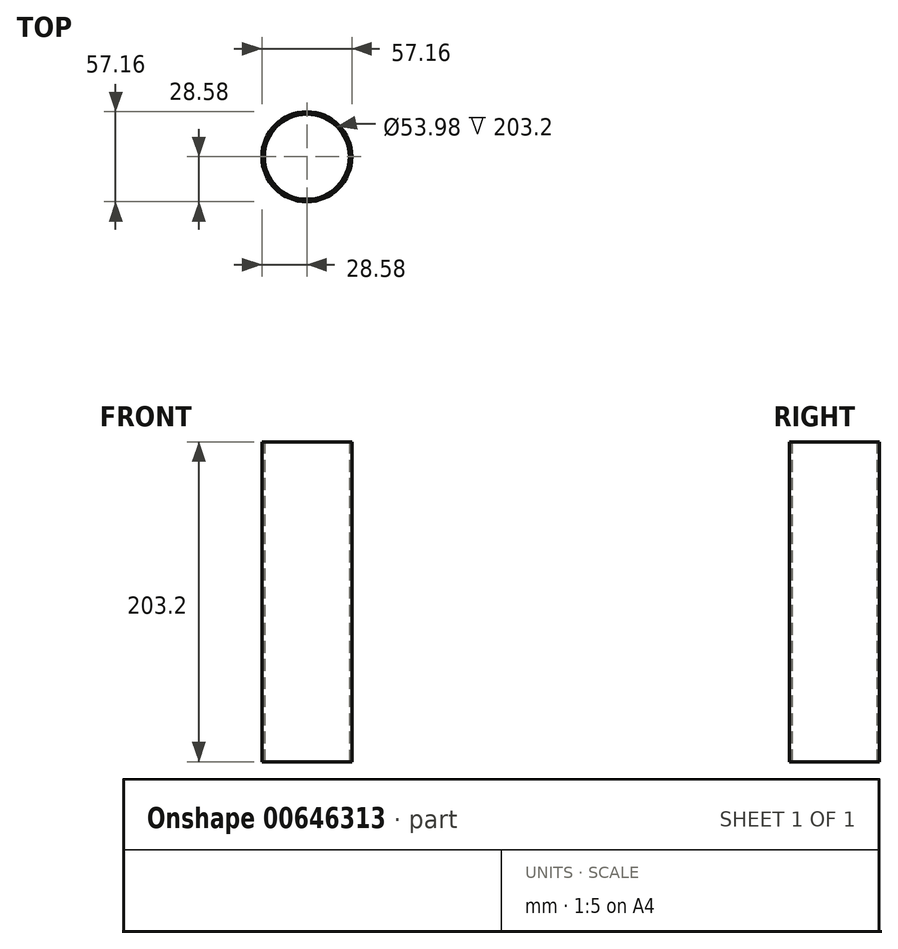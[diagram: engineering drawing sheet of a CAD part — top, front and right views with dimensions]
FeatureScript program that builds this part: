
annotation { "Feature Type Name" : "Feature", "Feature Type Description" : "" }
export const myFeature = defineFeature(function(context is Context, id is Id, definition is map)
    precondition{}
    {
        {
            var Q0;
            Q0=qCreatedBy(makeId("Top.planeOp"),FACE);
            var sketch = newSketch(context, id + "F0", { "sketchPlane" : qUnion([Q0])});
            skCircle(sketch, "E0", {"center": v(0, 0) * mm, "radius": 28.58 * mm});
            skCircle(sketch, "E1", {"center": v(0, 0) * mm, "radius": 26.99 * mm});
            skSolve(sketch);
        }
        {
            var Q0;
            Q0 = qSketchRegion(id + "F0", true);
            extrude(context, id + "F1", {"entities" : qUnion([Q0]), "depth" : 203.2 * mm, "offsetDistance" : 25.4 * mm});
        }
    });
